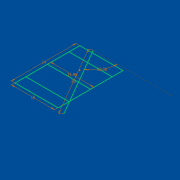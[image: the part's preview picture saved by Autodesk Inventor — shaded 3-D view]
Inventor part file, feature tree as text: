
AUTODESK INVENTOR PART (.ipt)
format: ipt  version: 2016 (Build 200138000, 138)  size: 64,512 bytes
history: native  units: mm
features: sketch x1
ambient origin geometry x8: Origin, YZ Plane, XZ Plane, XY Plane, X Axis, Y Axis, Z Axis, Center Point
feature tree (1):
  sketch  "Sketch1"  dims[d0=24.0mm d1=16.0mm d2=15.96mm d3=30.0mm d4=60.0deg]
